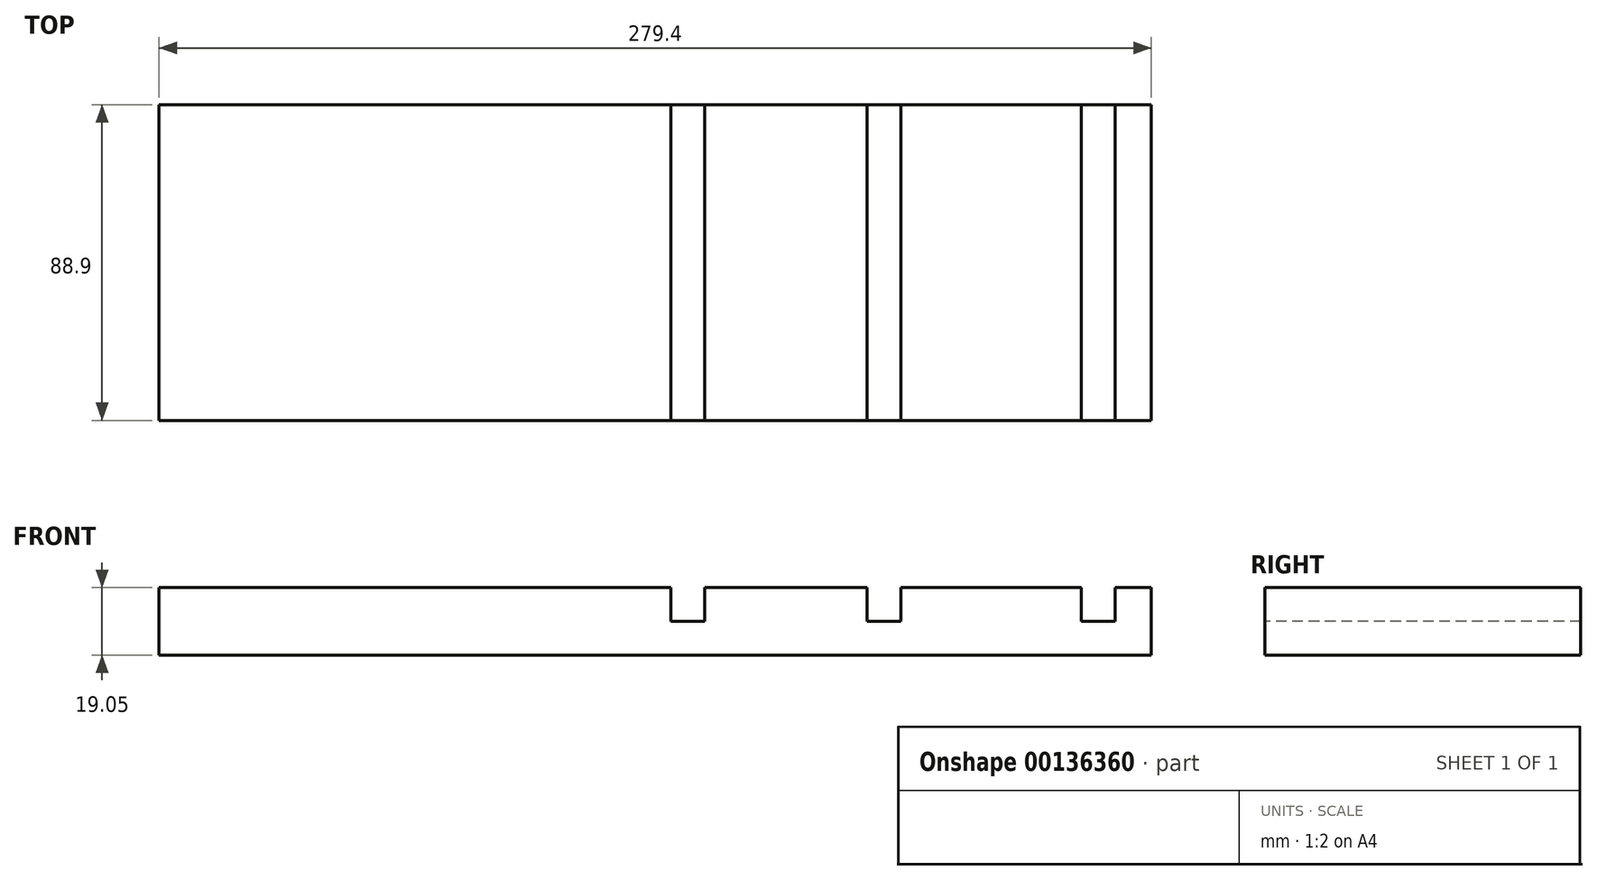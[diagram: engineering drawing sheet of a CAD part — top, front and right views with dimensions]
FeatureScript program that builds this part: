
annotation { "Feature Type Name" : "Feature", "Feature Type Description" : "" }
export const myFeature = defineFeature(function(context is Context, id is Id, definition is map)
    precondition{}
    {
        {
            var Q0;
            Q0=qCreatedBy(makeId("Front.planeOp"),FACE);
            var sketch = newSketch(context, id + "F0", { "sketchPlane" : qUnion([Q0])});
            skLineSegment(sketch, "E0.bottom", {"start": v(-134.68, -9.76) * mm, "end": v(144.72, -9.76) * mm});
            skLineSegment(sketch, "E0.top", {"start": v(-134.68, -28.8) * mm, "end": v(144.72, -28.8) * mm});
            skLineSegment(sketch, "E0.left", {"start": v(-134.68, -9.76) * mm, "end": v(-134.68, -28.8) * mm});
            skLineSegment(sketch, "E0.right", {"start": v(144.72, -9.76) * mm, "end": v(144.72, -28.8) * mm});
            skSolve(sketch);
        }
        {
            var Q0;
            Q0=makeQuery(id+"F0.imprint","IMPRINT",FACE,{"disambiguationData":[TD([[makeQuery(id+"F0.imprint","IMPRINT",EDGE,{"derivedFrom":sQuery(id+"F0.wireOp",EDGE,"E0.bottom")}),-1.0]])]});
            extrude(context, id + "F1", {"entities" : qUnion([Q0]), "depth" : 88.9 * mm});
        }
        {
            var Q0;
            Q0=makeQuery(id+"F1.opExtrude","SWEPT_FACE",FACE,{"disambiguationData":[OSD([sQuery(id+"F0.wireOp",EDGE,"E0.bottom")])]});
            var sketch = newSketch(context, id + "F2", { "sketchPlane" : qUnion([Q0])});
            skLineSegment(sketch, "E1.bottom", {"start": v(107.55, 0) * mm, "end": v(91.85, 0) * mm});
            skLineSegment(sketch, "E1.top", {"start": v(107.55, -88.9) * mm, "end": v(91.85, -88.9) * mm});
            skLineSegment(sketch, "E2.bottom", {"start": v(134.57, 0) * mm, "end": v(125.04, 0) * mm});
            skLineSegment(sketch, "E2.top", {"start": v(134.57, -88.9) * mm, "end": v(125.04, -88.9) * mm});
            skLineSegment(sketch, "E2.left", {"start": v(134.57, 0) * mm, "end": v(134.57, -88.9) * mm});
            skLineSegment(sketch, "E2.right", {"start": v(125.04, 0) * mm, "end": v(125.04, -88.9) * mm});
            skLineSegment(sketch, "E3", {"start": v(125.04, -39.22) * mm, "end": v(74.24, -39.22) * mm, "construction": true});
            skLineSegment(sketch, "E4.bottom", {"start": v(74.24, 0) * mm, "end": v(64.72, 0) * mm});
            skLineSegment(sketch, "E4.top", {"start": v(74.24, -88.9) * mm, "end": v(64.72, -88.9) * mm});
            skLineSegment(sketch, "E4.left", {"start": v(74.24, 0) * mm, "end": v(74.24, -88.9) * mm});
            skLineSegment(sketch, "E4.right", {"start": v(64.72, 0) * mm, "end": v(64.72, -88.9) * mm});
            skLineSegment(sketch, "E5", {"start": v(64.72, -39.87) * mm, "end": v(19, -39.87) * mm, "construction": true});
            skLineSegment(sketch, "E6.bottom", {"start": v(19, 0) * mm, "end": v(9.48, 0) * mm});
            skLineSegment(sketch, "E6.top", {"start": v(19, -88.9) * mm, "end": v(9.48, -88.9) * mm});
            skLineSegment(sketch, "E6.left", {"start": v(19, 0) * mm, "end": v(19, -88.9) * mm});
            skLineSegment(sketch, "E6.right", {"start": v(9.48, 0) * mm, "end": v(9.48, -88.9) * mm});
            skSolve(sketch);
        }
        {
            var Q0;
            Q0=makeQuery(id+"F2.imprint","IMPRINT",FACE,{"disambiguationData":[TD([[makeQuery(id+"F2.imprint","IMPRINT",EDGE,{"derivedFrom":sQuery(id+"F2.wireOp",EDGE,"E2.bottom")}),-1.0]])]});
            var Q1;
            Q1=makeQuery(id+"F2.imprint","IMPRINT",FACE,{"disambiguationData":[TD([[makeQuery(id+"F2.imprint","IMPRINT",EDGE,{"derivedFrom":sQuery(id+"F2.wireOp",EDGE,"E4.bottom")}),-1.0]])]});
            var Q2;
            Q2=makeQuery(id+"F2.imprint","IMPRINT",FACE,{"disambiguationData":[TD([[makeQuery(id+"F2.imprint","IMPRINT",EDGE,{"derivedFrom":sQuery(id+"F2.wireOp",EDGE,"E6.bottom")}),-1.0]])]});
            extrude(context, id + "F3", {"entities" : qUnion([Q0, Q1, Q2]), "operationType" : NewBodyOperationType.REMOVE, "oppositeDirection" : true, "depth" : 9.52 * mm});
        }
    });
